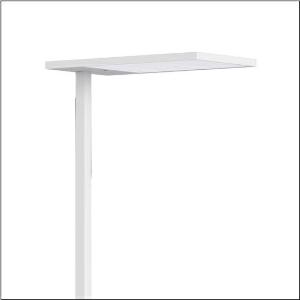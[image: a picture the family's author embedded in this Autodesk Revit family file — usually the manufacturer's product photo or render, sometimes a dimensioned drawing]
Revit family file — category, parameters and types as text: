
# Revit family: silica_21_floor_r_51mx53sg4ew
name_source: partatom
category: Lighting Fixtures
units: mm (PartAtom-declared; Revit-internal decimal feet)

## family parameters
Cut with Voids When Loaded = No
Host = Face
Light Source = No
Part Type = Normal
Room Calculation Point = No
Round Connector Dimension = Use Diameter
Shared = No

## types (1)
- Silica 21 Floor R (1 x LED, 15000 lm, 106.4 W, 4000K)
    Apparent Load = 106 VA
    CIE Flux Codes = 54 86 97 13 100
    Color Rendering = 80
    Color Temperature = 4000K
    Default Elevation = 1800 mm
    Description = Silica® 21 Floor R, floorstanding luminaire, of PMMA, primary optical cover: prismatic diffuser, of PMMA, CAT 2 (L<= 3000cd/m²), light emission: indirect/direct distribution, primary light characteristic: symmetric, primary optical cover: cover panel, of PMMA, installation type: not mounted, LED, rated luminous flux: 15.000lm, luminous efficacy: 141lm/W, light colour: 840, colour temperature: 4000K, control gear: DALI 2, daylight-dependent control, mains connection: 230V, AC, 50/60Hz, connection cable included, cable length: 2,5m, rated input power: 106.4W, luminaire head, of aluminium, powder-coated, traffic white (RAL 9016), length: 671mm, width: 371mm, height: 2010mm, supporting column, angular, of aluminium, powder-coated, traffic white (RAL 9016), baseplate, of steel, powder-coated, traffic white (RAL 9016), sensor module PR3-S, local control - self-sufficient standalone sensors, equipment: master, direct and indirect component separately switchable, protection rating (complete): IP20, insulation class (complete): insulation class I (protective earthing), certification: CE, permissible operating ambient temperature: 0..+35°C, standard: EN 50419, packaging unit: 1 piece
    Height = 18 mm
    Lamp = 1 x LED
    Lamp Light Flux = 15000 lm
    Lamp Power = 106.4 W
    Lamp count = 1
    Length = 650 mm
    Luminous efficacy = 141 lm/W
    Manufacturer = Siteco
    ModVariant = No
    Model = 51MX53SG4EW
    Mounting Place = Floor
    Mounting Type = Freestanding
    Number of Poles = 1
    OnlyDefault = Yes
    Power Factor = 1
    Product Name = Silica 21 Floor R
    Product group = floorstanding luminaire
    ProductGroupID = 1302
    Protection Class = Protection class I
    Protection Degree = IP 20
    RLX_Detail_Level = 1
    RLX_Emergency_Light_Flux = 0 lm
    RLX_Emergency_Type = 0
    RLX_Emergency_Type_DB = No
    RlxData = <blob elided: 18917 chars, md5=3183f146>
    Socket = socket
    Standby Power = 0 W
    System Light Flux = 15000 lm
    System Power = 106 W
    Type Comments = Product without accessories
    Type Image = l_1003935.jpg
    URL = http://relux.com
    VarID = ---
    Voltage = 0 V
    Weight = 0.00 kg
    Width = 350 mm

## geometry (parser evidence)
native form markers: Blend x4, Sweep x13
no freeform markers — native parametric forms only
